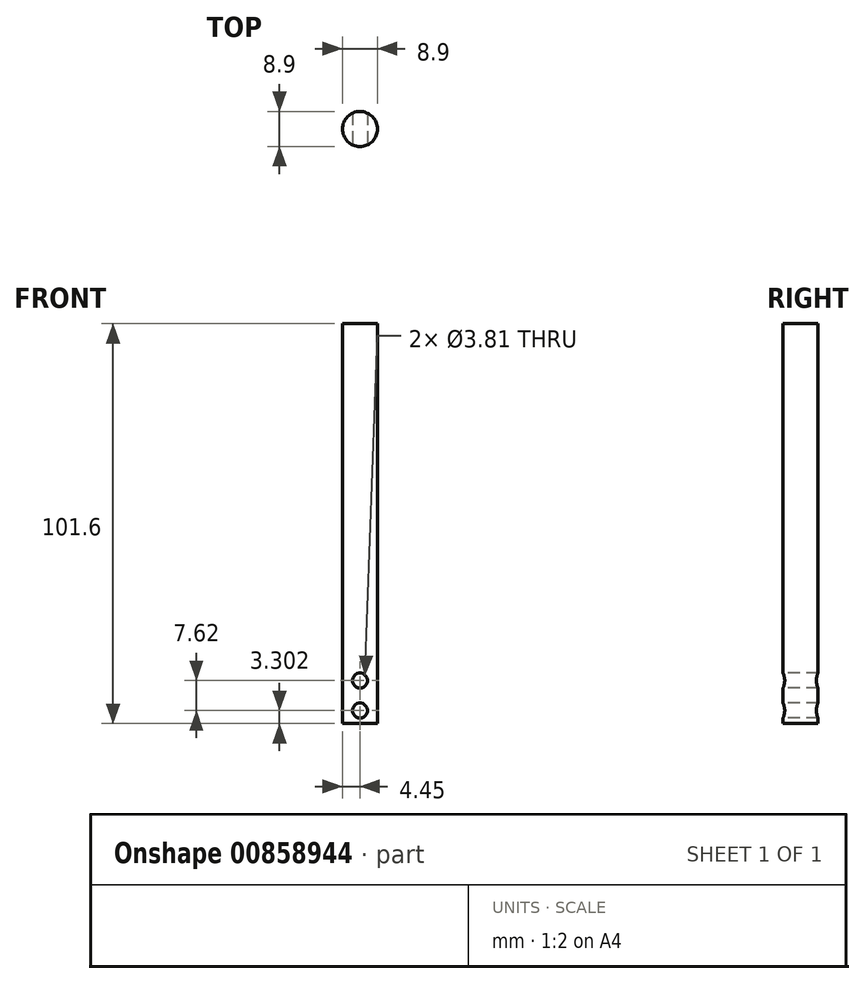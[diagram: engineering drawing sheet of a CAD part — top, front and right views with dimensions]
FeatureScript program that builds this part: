
annotation { "Feature Type Name" : "Feature", "Feature Type Description" : "" }
export const myFeature = defineFeature(function(context is Context, id is Id, definition is map)
    precondition{}
    {
        {
            var Q0;
            Q0=qCreatedBy(makeId("Top.planeOp"),FACE);
            var sketch = newSketch(context, id + "F0", { "sketchPlane" : qUnion([Q0])});
            skCircle(sketch, "E0", {"center": v(0, 0) * mm, "radius": 4.45 * mm});
            skSolve(sketch);
        }
        {
            var Q0;
            Q0=qSketchRegion(id+"F0",true);
            extrude(context, id + "F1", {"entities" : qUnion([Q0]), "depth" : 101.6 * mm, "offsetDistance" : 25.4 * mm});
        }
        {
            var Q0;
            Q0=qCreatedBy(makeId("Front.planeOp"),FACE);
            var sketch = newSketch(context, id + "F2", { "sketchPlane" : qUnion([Q0])});
            skCircle(sketch, "E1", {"center": v(0, 3.3) * mm, "radius": 1.9 * mm});
            skCircle(sketch, "E2", {"center": v(0, 10.92) * mm, "radius": 1.9 * mm});
            skSolve(sketch);
        }
        {
            var Q0;
            Q0=qSketchRegion(id+"F2",true);
            extrude(context, id + "F3", {"entities" : qUnion([Q0]), "operationType" : NewBodyOperationType.REMOVE, "endBound" : BoundingType.THROUGH_ALL, "oppositeDirection" : true, "depth" : 25.4 * mm, "offsetDistance" : 25.4 * mm, "hasSecondDirection" : true, "secondDirectionOppositeDirection" : false, "secondDirectionDepth" : 12.7 * mm});
        }
    });
